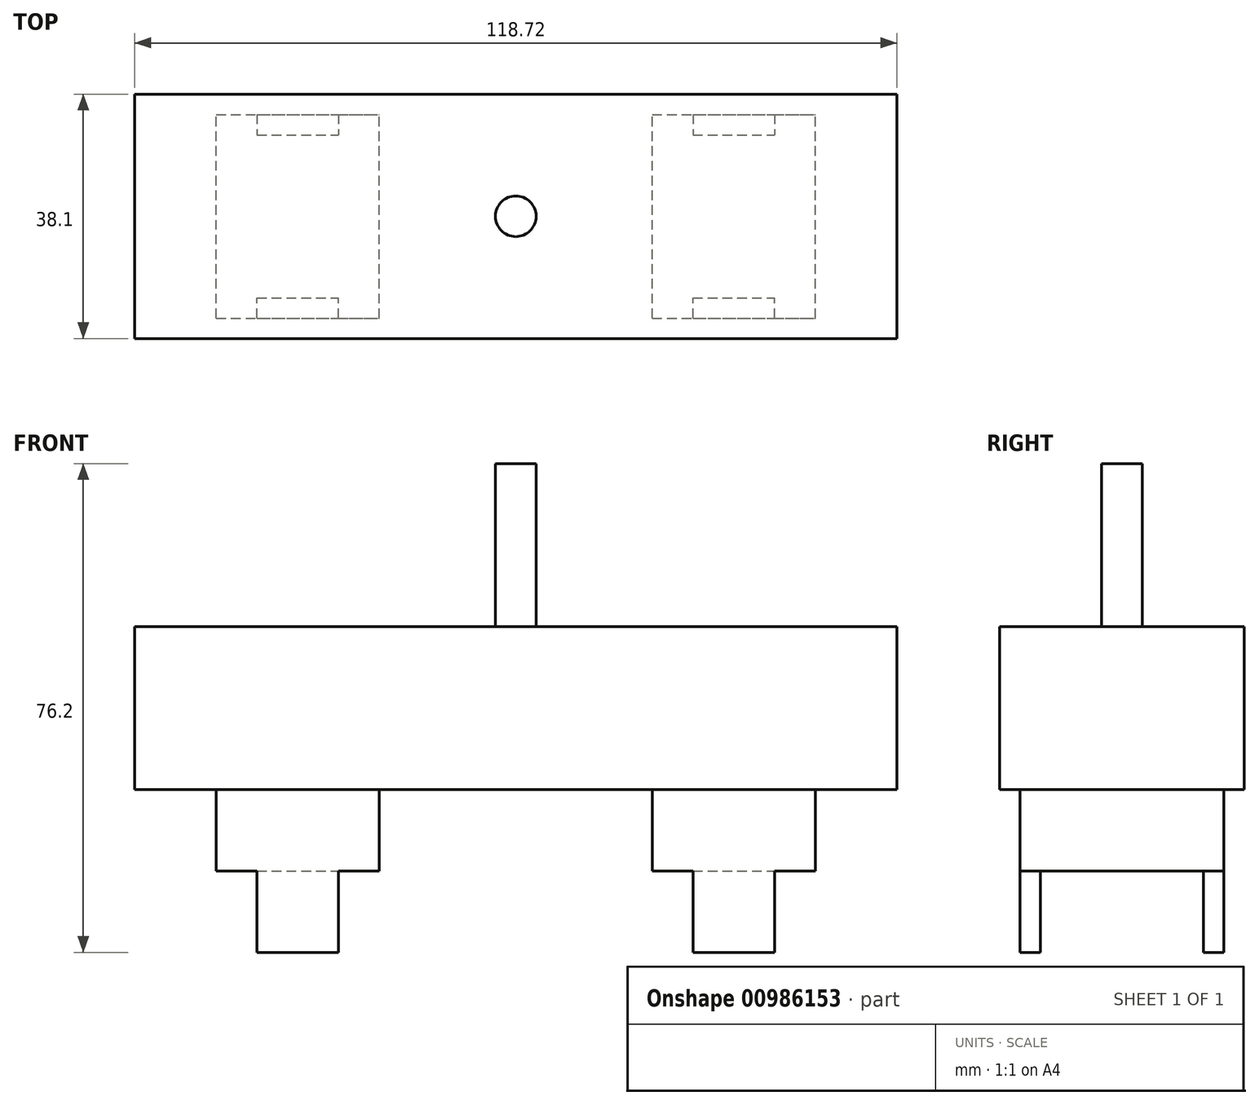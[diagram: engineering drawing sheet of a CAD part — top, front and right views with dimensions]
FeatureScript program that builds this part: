
annotation { "Feature Type Name" : "Feature", "Feature Type Description" : "" }
export const myFeature = defineFeature(function(context is Context, id is Id, definition is map)
    precondition{}
    {
        {
            var Q0;
            Q0=qCreatedBy(makeId("Top.planeOp"),FACE);
            var sketch = newSketch(context, id + "F0", { "sketchPlane" : qUnion([Q0])});
            skLineSegment(sketch, "E0.bottom", {"start": v(-59.36, 19.05) * mm, "end": v(59.36, 19.05) * mm});
            skLineSegment(sketch, "E0.top", {"start": v(-59.36, -19.05) * mm, "end": v(59.36, -19.05) * mm});
            skLineSegment(sketch, "E0.left", {"start": v(-59.36, 19.05) * mm, "end": v(-59.36, -19.05) * mm});
            skLineSegment(sketch, "E0.right", {"start": v(59.36, 19.05) * mm, "end": v(59.36, -19.05) * mm});
            skPoint(sketch, "E0.middle", {"position": v(0, 0) * mm});
            skSolve(sketch);
        }
        {
            var Q0;
            Q0 = qSketchRegion(id + "F0", true);
            extrude(context, id + "F1", {"entities" : qUnion([Q0]), "depth" : 25.4 * mm, "offsetDistance" : 25.4 * mm});
        }
        {
            var Q0;
            Q0=makeQuery(id+"F1.opExtrude","CAP_FACE",FACE,{"disambiguationData":[OSD([sQuery(id+"F0.wireOp",EDGE,"E0.bottom"),sQuery(id+"F0.wireOp",EDGE,"E0.top"),sQuery(id+"F0.wireOp",EDGE,"E0.left"),sQuery(id+"F0.wireOp",EDGE,"E0.right")])],"isStart":true});
            var sketch = newSketch(context, id + "F2", { "sketchPlane" : qUnion([Q0])});
            skLineSegment(sketch, "E1.bottom", {"start": v(-46.66, 15.88) * mm, "end": v(-21.26, 15.88) * mm});
            skLineSegment(sketch, "E1.top", {"start": v(-46.66, -15.87) * mm, "end": v(-21.26, -15.87) * mm});
            skLineSegment(sketch, "E1.left", {"start": v(-46.66, 15.88) * mm, "end": v(-46.66, -15.87) * mm});
            skLineSegment(sketch, "E1.right", {"start": v(-21.26, 15.88) * mm, "end": v(-21.26, -15.87) * mm});
            skLineSegment(sketch, "E2.bottom", {"start": v(21.26, 15.88) * mm, "end": v(46.66, 15.88) * mm});
            skLineSegment(sketch, "E2.top", {"start": v(21.26, -15.87) * mm, "end": v(46.66, -15.87) * mm});
            skLineSegment(sketch, "E2.left", {"start": v(21.26, 15.88) * mm, "end": v(21.26, -15.87) * mm});
            skLineSegment(sketch, "E2.right", {"start": v(46.66, 15.88) * mm, "end": v(46.66, -15.87) * mm});
            skSolve(sketch);
        }
        {
            var Q0;
            Q0 = qSketchRegion(id + "F2", true);
            extrude(context, id + "F3", {"entities" : qUnion([Q0]), "operationType" : NewBodyOperationType.ADD, "depth" : 12.7 * mm, "offsetDistance" : 25.4 * mm});
        }
        {
            var Q0;
            Q0=makeQuery(id+"F3.opExtrude","CAP_FACE",FACE,{"disambiguationData":[OSD([sQuery(id+"F2.wireOp",EDGE,"E1.bottom"),sQuery(id+"F2.wireOp",EDGE,"E1.top"),sQuery(id+"F2.wireOp",EDGE,"E1.left"),sQuery(id+"F2.wireOp",EDGE,"E1.right")])],"isStart":false});
            var sketch = newSketch(context, id + "F4", { "sketchPlane" : qUnion([Q0])});
            skLineSegment(sketch, "E3.bottom", {"start": v(-40.3, 15.88) * mm, "end": v(-27.6, 15.88) * mm});
            skLineSegment(sketch, "E3.top", {"start": v(-40.3, 12.7) * mm, "end": v(-27.6, 12.7) * mm});
            skLineSegment(sketch, "E3.left", {"start": v(-40.3, 15.88) * mm, "end": v(-40.3, 12.7) * mm});
            skLineSegment(sketch, "E3.right", {"start": v(-27.6, 15.88) * mm, "end": v(-27.6, 12.7) * mm});
            skLineSegment(sketch, "E4.bottom", {"start": v(-40.3, -15.87) * mm, "end": v(-27.6, -15.87) * mm});
            skLineSegment(sketch, "E4.top", {"start": v(-40.3, -12.7) * mm, "end": v(-27.6, -12.7) * mm});
            skLineSegment(sketch, "E4.left", {"start": v(-40.3, -15.87) * mm, "end": v(-40.3, -12.7) * mm});
            skLineSegment(sketch, "E4.right", {"start": v(-27.6, -15.87) * mm, "end": v(-27.6, -12.7) * mm});
            skSolve(sketch);
        }
        {
            var Q0;
            Q0 = qSketchRegion(id + "F4", true);
            extrude(context, id + "F5", {"entities" : qUnion([Q0]), "operationType" : NewBodyOperationType.ADD, "depth" : 12.7 * mm, "offsetDistance" : 25.4 * mm});
        }
        {
            var Q0;
            Q0=makeQuery(id+"F3.opExtrude","CAP_FACE",FACE,{"disambiguationData":[OSD([sQuery(id+"F2.wireOp",EDGE,"E2.bottom"),sQuery(id+"F2.wireOp",EDGE,"E2.top"),sQuery(id+"F2.wireOp",EDGE,"E2.left"),sQuery(id+"F2.wireOp",EDGE,"E2.right")])],"isStart":false});
            var sketch = newSketch(context, id + "F6", { "sketchPlane" : qUnion([Q0])});
            skLineSegment(sketch, "E5.bottom", {"start": v(27.6, 15.88) * mm, "end": v(40.3, 15.88) * mm});
            skLineSegment(sketch, "E5.top", {"start": v(27.6, 12.7) * mm, "end": v(40.3, 12.7) * mm});
            skLineSegment(sketch, "E5.left", {"start": v(27.6, 15.88) * mm, "end": v(27.6, 12.7) * mm});
            skLineSegment(sketch, "E5.right", {"start": v(40.3, 15.88) * mm, "end": v(40.3, 12.7) * mm});
            skLineSegment(sketch, "E6.bottom", {"start": v(27.6, -15.87) * mm, "end": v(40.3, -15.87) * mm});
            skLineSegment(sketch, "E6.top", {"start": v(27.6, -12.7) * mm, "end": v(40.3, -12.7) * mm});
            skLineSegment(sketch, "E6.left", {"start": v(27.6, -15.87) * mm, "end": v(27.6, -12.7) * mm});
            skLineSegment(sketch, "E6.right", {"start": v(40.3, -15.87) * mm, "end": v(40.3, -12.7) * mm});
            skSolve(sketch);
        }
        {
            var Q0;
            Q0 = qSketchRegion(id + "F6", true);
            extrude(context, id + "F7", {"entities" : qUnion([Q0]), "operationType" : NewBodyOperationType.ADD, "depth" : 12.7 * mm, "offsetDistance" : 25.4 * mm});
        }
        {
            var Q0;
            Q0=makeQuery(id+"F1.opExtrude","CAP_FACE",FACE,{"disambiguationData":[OSD([sQuery(id+"F0.wireOp",EDGE,"E0.bottom"),sQuery(id+"F0.wireOp",EDGE,"E0.top"),sQuery(id+"F0.wireOp",EDGE,"E0.left"),sQuery(id+"F0.wireOp",EDGE,"E0.right")])],"isStart":false});
            var sketch = newSketch(context, id + "F8", { "sketchPlane" : qUnion([Q0])});
            skCircle(sketch, "E7", {"center": v(0, 0) * mm, "radius": 3.18 * mm});
            skSolve(sketch);
        }
        {
            var Q0;
            Q0 = qSketchRegion(id + "F8", true);
            extrude(context, id + "F9", {"entities" : qUnion([Q0]), "operationType" : NewBodyOperationType.ADD, "depth" : 25.4 * mm, "offsetDistance" : 25.4 * mm});
        }
    });
